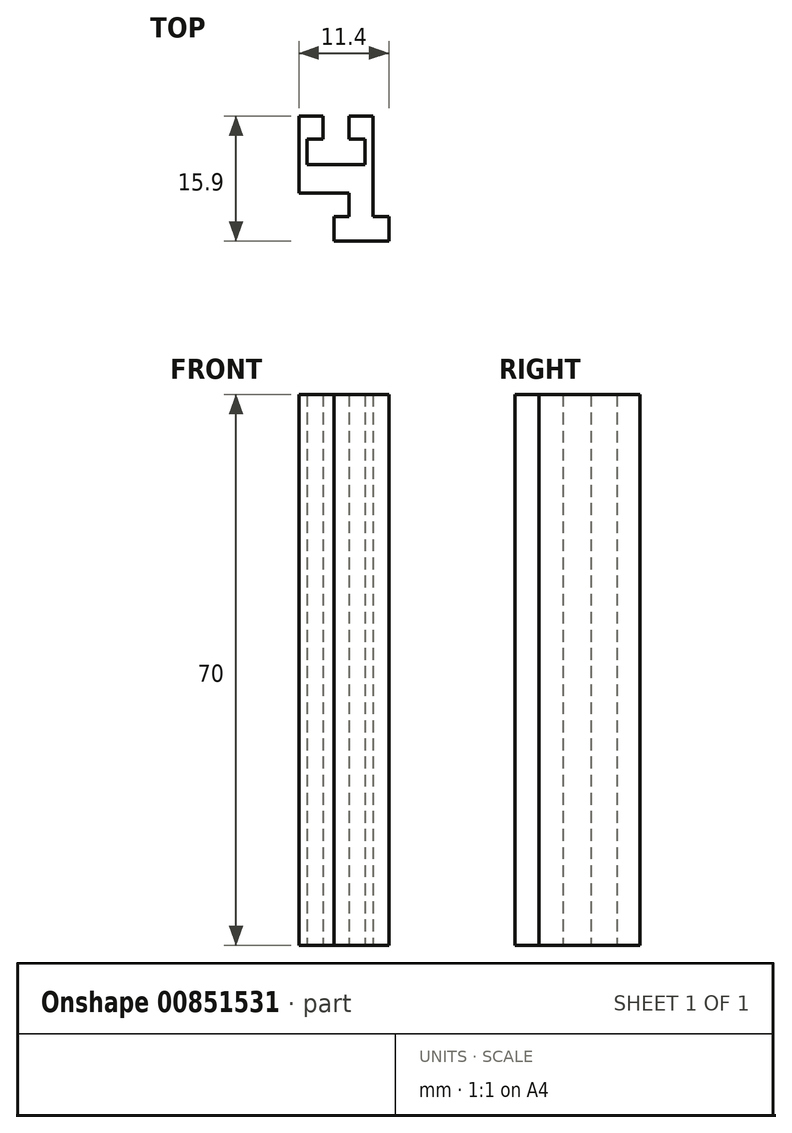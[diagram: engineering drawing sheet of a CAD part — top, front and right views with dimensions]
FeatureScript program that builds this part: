
annotation { "Feature Type Name" : "Feature", "Feature Type Description" : "" }
export const myFeature = defineFeature(function(context is Context, id is Id, definition is map)
    precondition{}
    {
        {
            var Q0;
            Q0=qCreatedBy(makeId("Top.planeOp"),FACE);
            var sketch = newSketch(context, id + "F0", { "sketchPlane" : qUnion([Q0])});
            skLineSegment(sketch, "E0.1", {"start": v(-35.18, -2.96) * mm, "end": v(-33.13, -2.96) * mm});
            skLineSegment(sketch, "E0.2", {"start": v(-33.13, -2.96) * mm, "end": v(-33.13, -6.23) * mm});
            skLineSegment(sketch, "E0.4", {"start": v(-40.53, -2.94) * mm, "end": v(-38.51, -2.94) * mm});
            skLineSegment(sketch, "E0.5", {"start": v(-40.53, -2.94) * mm, "end": v(-40.53, -6.23) * mm});
            skLineSegment(sketch, "E0.6", {"start": v(-40.53, -6.23) * mm, "end": v(-33.13, -6.23) * mm});
            skLineSegment(sketch, "E1", {"start": v(-38.51, -2.94) * mm, "end": v(-38.51, -0.02) * mm});
            skLineSegment(sketch, "E2", {"start": v(-38.51, -0.02) * mm, "end": v(-41.53, -0.02) * mm});
            skLineSegment(sketch, "E3", {"start": v(-41.53, -0.02) * mm, "end": v(-41.53, -9.82) * mm});
            skLineSegment(sketch, "E4", {"start": v(-37.08, -15.92) * mm, "end": v(-30.13, -15.92) * mm});
            skLineSegment(sketch, "E5", {"start": v(-32.13, -9.77) * mm, "end": v(-32.13, -0.02) * mm});
            skLineSegment(sketch, "E6", {"start": v(-32.13, -0.02) * mm, "end": v(-35.18, -0.02) * mm});
            skLineSegment(sketch, "E7", {"start": v(-35.18, -0.02) * mm, "end": v(-35.18, -2.96) * mm});
            skLineSegment(sketch, "E8.left", {"start": v(-35.18, -9.82) * mm, "end": v(-35.18, -12.82) * mm});
            skLineSegment(sketch, "E8.right", {"start": v(-32.13, -9.77) * mm, "end": v(-32.13, -12.82) * mm});
            skLineSegment(sketch, "E9.bottom", {"start": v(-37.08, -12.82) * mm, "end": v(-35.18, -12.82) * mm});
            skLineSegment(sketch, "E9.left", {"start": v(-37.08, -12.82) * mm, "end": v(-37.08, -15.92) * mm});
            skLineSegment(sketch, "E9.right", {"start": v(-30.13, -12.82) * mm, "end": v(-30.13, -15.92) * mm});
            skLineSegment(sketch, "E10.trimOffspring", {"start": v(-32.13, -12.82) * mm, "end": v(-30.13, -12.82) * mm});
            skPoint(sketch, "E11", {"position": v(-36.83, -6.23) * mm});
            skLineSegment(sketch, "E12", {"start": v(-35.18, -9.82) * mm, "end": v(-41.53, -9.82) * mm});
            skLineSegment(sketch, "E13", {"start": v(-32.13, -9.77) * mm, "end": v(-32.13, -9.77) * mm});
            skSolve(sketch);
        }
        {
            var Q0;
            Q0=makeQuery(id+"F0.imprint","IMPRINT",FACE,{"disambiguationData":[TD([[makeQuery(id+"F0.imprint","IMPRINT",EDGE,{"derivedFrom":sQuery(id+"F0.wireOp",EDGE,"E0.1")}),1.0]])]});
            extrude(context, id + "F1", {"entities" : qUnion([Q0]), "endBound" : BoundingType.SYMMETRIC, "depth" : 70 * mm, "offsetDistance" : 25 * mm});
        }
    });
